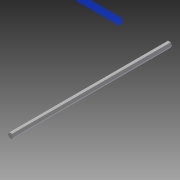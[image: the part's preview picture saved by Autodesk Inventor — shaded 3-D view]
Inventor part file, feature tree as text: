
AUTODESK INVENTOR PART (.ipt)
format: ipt  version: 2014 SP1 (Build 180222100, 222)  size: 74,240 bytes
history: native  units: in
note: dims shown in document units (in); Inventor stores cm internally (conversion verified against a paired STEP export)
features: extrude x1, sketch x1
ambient origin geometry x8: Origin, YZ Plane, XZ Plane, XY Plane, X Axis, Y Axis, Z Axis, Center Point
bodies: Solid1 (feature_tree)
feature tree (2):
  extrude  "Extrusion1"  Depth=17.0in TaperAngle=0.0deg
  sketch  "Sketch1"  dims[d0=0.5in d1=17.0in d2=0.0in]
